# Revit family: BVN_BRCF
name_source: partatom
category: Mechanical Equipment
units: mm (PartAtom-declared; Revit-internal decimal feet)

## family parameters
Cut with Voids When Loaded = No
Host = Face
Part Type = Normal
Room Calculation Point = No
Round Connector Dimension = Use Diameter
Shared = No

## types (17) — shared parameters
Default Elevation = 1219 mm
Description = Roof Fan
E' = 650 mm
Frequency = 50 Hz
Insulation Class = F
Manufacturer = Bahçıvan Elektrik Motor San. ve Tic. Ltd. Şti.
Material = <By Category>
Model = BRCF
Protection Class = 55
URL = http://www.bahcivanmotor.com.tr

## per-type parameters (varying)
| type | A | Air Flow | B | C | Capacitor | Current | D | D' | E | G | Kh | Power | Q | Qh | Sound Pressure Level dB(A) | Speed(d/d) | Voltage | Weight |
| BRCF 280M | 522 mm | 1000.0 m³/h | 495 mm | 165 mm | 10 | 2 A | 180 mm  [stored 0.590551 ft] | 200 mm | 404 mm  [stored 1.32546 ft] | 30 mm  [stored 0.0984252 ft] | 310 mm  [stored 1.01706 ft] | 250 W | 394 mm  [stored 1.29265 ft] | 135 mm  [stored 0.442913 ft] | 53 | 1390 | 230 V | 35.00 kg |
| BRCF 315M | 595 mm | 1950.0 m³/h | 555 mm | 198 mm  [stored 0.649606 ft] | 10 | 2 A | 220 mm  [stored 0.721785 ft] | 240 mm  [stored 0.787402 ft] | 454 mm | 30 mm  [stored 0.0984252 ft] | 345 mm  [stored 1.13189 ft] | 250 W | 444 mm  [stored 1.45669 ft] | 160 mm  [stored 0.524934 ft] | 53 | 1380 | 230 V | 42.00 kg |
| BRCF 355M | 656 mm | 2900.0 m³/h | 555 mm | 234 mm  [stored 0.767717 ft] | 10 | 2 A | 225 mm  [stored 0.738189 ft] | 245 mm  [stored 0.803806 ft] | 500 mm | 30 mm  [stored 0.0984252 ft] | 345 mm  [stored 1.13189 ft] | 250 W | 490 mm | 160 mm  [stored 0.524934 ft] | 55 | 1380 | 230 V | 50.00 kg |
| BRCF 400M | 656 mm | 4000.0 m³/h | 585 mm | 268 mm | 15 | 3 A | 225 mm  [stored 0.738189 ft] | 245 mm  [stored 0.803806 ft] | 500 mm | 30 mm  [stored 0.0984252 ft] | 365 mm  [stored 1.19751 ft] | 370 W | 490 mm | 170 mm  [stored 0.557743 ft] | 60 | 1390 | 230 V | 55.00 kg |
| BRCF 450M | 656 mm | 5550.0 m³/h | 616 mm | 303 mm  [stored 0.994094 ft] | 20 | 5 A | 265 mm  [stored 0.869423 ft] | 285 mm  [stored 0.935039 ft] | 580 mm | 44 mm  [stored 0.144357 ft] | 375 mm  [stored 1.23031 ft] | 550 W | 570 mm | 177 mm  [stored 0.580709 ft] | 62 | 1365 | 230 V | 62.00 kg |
| BRCF 500M | 766 mm | 8300.0 m³/h | 660 mm | 342 mm  [stored 1.12205 ft] | 35 | 8 A | 295 mm  [stored 0.967848 ft] | 315 mm  [stored 1.03346 ft] | 640 mm | 44 mm  [stored 0.144357 ft] | 406 mm  [stored 1.33202 ft] | 1100 W | 630 mm | 190 mm | 64 | 1410 | 230 V | 68.00 kg |
| BRCF 560M | 828 mm | 10800.0 m³/h | 723 mm | 380 mm | 50 | 14 A | 325 mm  [stored 1.06627 ft] | 345 mm  [stored 1.13189 ft] | 700 mm | 44 mm  [stored 0.144357 ft] | 448 mm | 2 W | 690 mm | 211 mm  [stored 0.692257 ft] | 66 | 1420 | 230 V | 75.00 kg |
| BRCF 630T | 997 mm | 13000.0 m³/h | 922 mm | 445 mm | 0 | 7 A | 400 mm  [stored 1.31234 ft] | 420 mm  [stored 1.37795 ft] | 730 mm | 54 mm  [stored 0.177165 ft] | 563 mm | 3000 W | 720 mm | 285 mm  [stored 0.935039 ft] | 60 | 1000 | 380 V | 127.00 kg |
| BRCF 710T | 1095 mm | 15000.0 m³/h | 991 mm | 500 mm | 0 | 8 A | 425 mm  [stored 1.39436 ft] | 445 mm | 780 mm | 54 mm  [stored 0.177165 ft] | 609 mm | 4000 W | 770 mm | 308 mm  [stored 1.0105 ft] | 63 | 1000 | 380 V | 150.00 kg |
| BRCF 800T | 1205 mm | 17000.0 m³/h | 1172 mm | 542 mm | 0 | 15 A | 450 mm | 470 mm | 900 mm | 54 mm  [stored 0.177165 ft] | 709 mm | 7500 W | 890 mm | 389 mm  [stored 1.27625 ft] | 67 | 1000 | 380 V | 216.00 kg |
| BRCF 280T | 522 mm | 1000.0 m³/h | 495 mm | 165 mm | 0 | 1 A | 180 mm  [stored 0.590551 ft] | 200 mm | 404 mm  [stored 1.32546 ft] | 30 mm  [stored 0.0984252 ft] | 310 mm  [stored 1.01706 ft] | 250 W | 394 mm  [stored 1.29265 ft] | 135 mm  [stored 0.442913 ft] | 53 | 1380 | 380 V | 35.00 kg |
| BRCF 315T | 595 mm | 1950.0 m³/h | 555 mm | 198 mm  [stored 0.649606 ft] | 0 | 1 A | 220 mm  [stored 0.721785 ft] | 240 mm  [stored 0.787402 ft] | 454 mm | 30 mm  [stored 0.0984252 ft] | 345 mm  [stored 1.13189 ft] | 250 W | 444 mm  [stored 1.45669 ft] | 160 mm  [stored 0.524934 ft] | 53 | 1380 | 380 V | 42.00 kg |
| BRCF 355T | 656 mm | 2900.0 m³/h | 555 mm | 234 mm  [stored 0.767717 ft] | 0 | 1 A | 225 mm  [stored 0.738189 ft] | 245 mm  [stored 0.803806 ft] | 500 mm | 30 mm  [stored 0.0984252 ft] | 345 mm  [stored 1.13189 ft] | 250 W | 490 mm | 160 mm  [stored 0.524934 ft] | 55 | 1380 | 380 V | 50.00 kg |
| BRCF 400T | 656 mm | 4000.0 m³/h | 585 mm | 268 mm | 0 | 1 A | 225 mm  [stored 0.738189 ft] | 245 mm  [stored 0.803806 ft] | 500 mm | 30 mm  [stored 0.0984252 ft] | 365 mm  [stored 1.19751 ft] | 370 W | 490 mm | 170 mm  [stored 0.557743 ft] | 60 | 1390 | 380 V | 55.00 kg |
| BRCF 450T | 656 mm | 5550.0 m³/h | 616 mm | 303 mm  [stored 0.994094 ft] | 0 | 2 A | 265 mm  [stored 0.869423 ft] | 285 mm  [stored 0.935039 ft] | 580 mm | 44 mm  [stored 0.144357 ft] | 375 mm  [stored 1.23031 ft] | 550 W | 570 mm | 177 mm  [stored 0.580709 ft] | 62 | 1365 | 380 V | 62.00 kg |
| BRCF 500T | 766 mm | 8300.0 m³/h | 660 mm | 342 mm  [stored 1.12205 ft] | 0 | 3 A | 295 mm  [stored 0.967848 ft] | 315 mm  [stored 1.03346 ft] | 640 mm | 44 mm  [stored 0.144357 ft] | 406 mm  [stored 1.33202 ft] | 1100 W | 630 mm | 190 mm | 64 | 1410 | 380 V | 68.00 kg |
| BRCF 560T | 828 mm | 10800.0 m³/h | 723 mm | 380 mm | 0 | 5 A | 325 mm  [stored 1.06627 ft] | 345 mm  [stored 1.13189 ft] | 700 mm | 44 mm  [stored 0.144357 ft] | 448 mm | 2200 W | 690 mm | 211 mm  [stored 0.692257 ft] | 66 | 1420 | 380 V | 75.00 kg |

note: [stored X ft] marks values corroborated as IEEE doubles in the binary element streams (Revit-internal decimal feet)

## geometry (parser evidence)
native form markers: Sweep x2
no freeform markers — native parametric forms only
